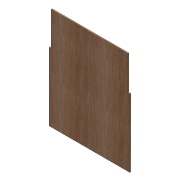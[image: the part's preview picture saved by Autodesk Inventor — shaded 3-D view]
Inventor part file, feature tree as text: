
AUTODESK INVENTOR PART (.ipt)
format: ipt  version: 2012 (Build 160160000, 160)  size: 120,832 bytes
history: native  units: in
note: dims shown in document units (in); Inventor stores cm internally (conversion verified against a paired STEP export)
features: extrude x3, sketch x3
ambient origin geometry x8: Origin, YZ Plane, XZ Plane, XY Plane, X Axis, Y Axis, Z Axis, Center Point
bodies: Solid1 (feature_tree)
feature tree (6):
  extrude  "Extrusion1"  Depth=19.0in
  extrude  "Extrusion2"  Depth=0.25in
  extrude  "Extrusion3"  Depth=0.5in
  sketch  "Sketch1"  dims[d0=22.0in d1=19.0in]
  sketch  "Sketch2"  dims[d2=0.25in d3=0.25in]
  sketch  "Sketch3"  dims[d4=0.5in d5=0.5in d7=0.5in d8=0.5in d9=0.25in d10=0.0in d13=1.0in d14=1.0in d15=0.0in d16=6.0in d17=0.25in d18=0.25in d19=0.5in d20=0.5in d21=0.5in d22=0.5in d23=1.0in d24=0.0in]
